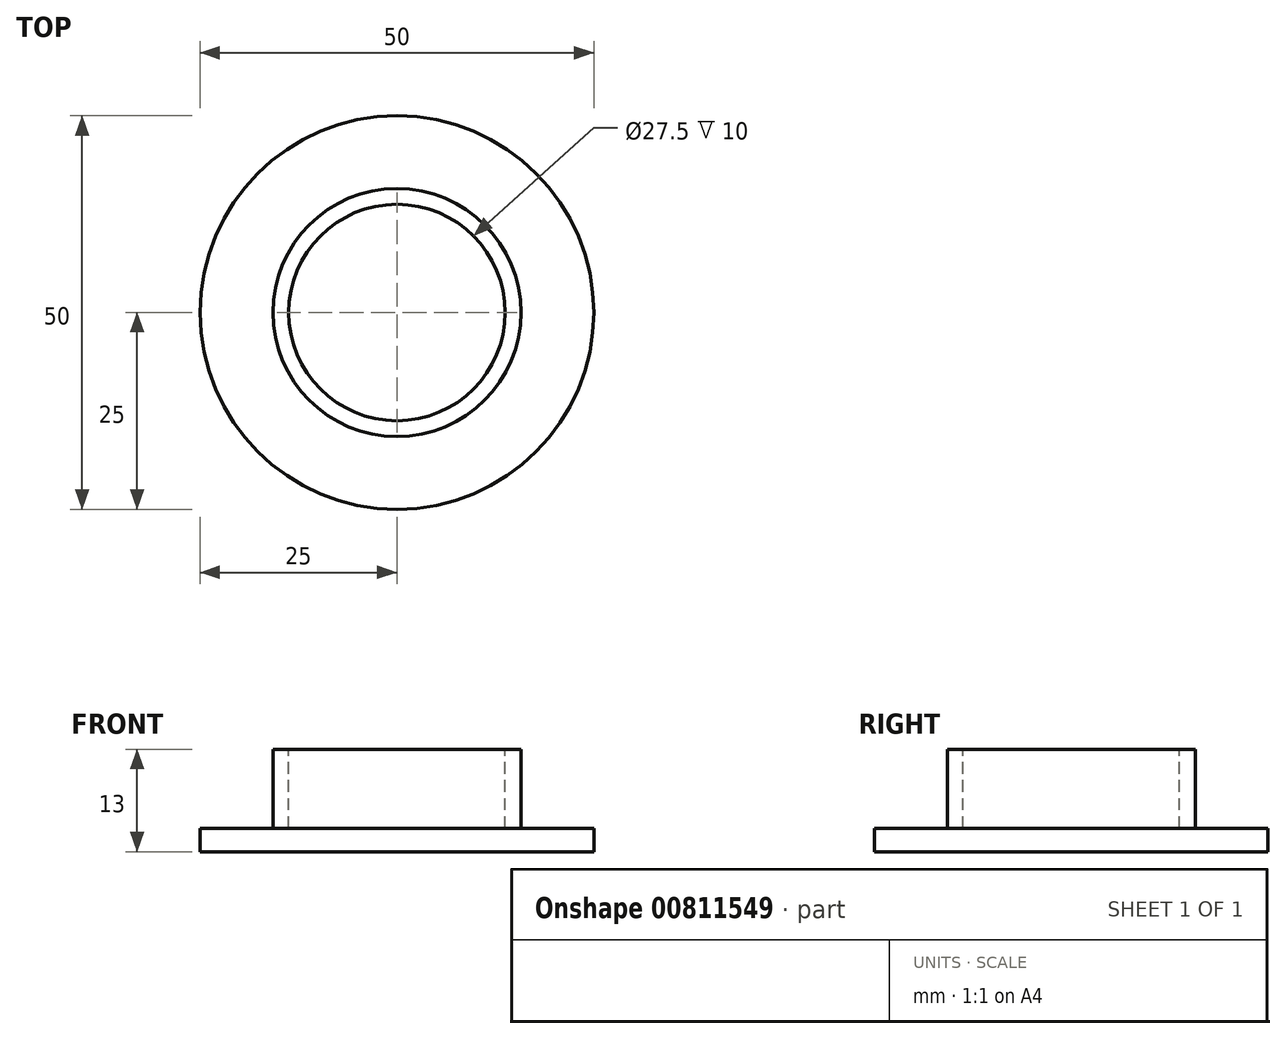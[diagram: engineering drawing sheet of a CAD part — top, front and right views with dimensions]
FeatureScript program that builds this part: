
annotation { "Feature Type Name" : "Feature", "Feature Type Description" : "" }
export const myFeature = defineFeature(function(context is Context, id is Id, definition is map)
    precondition{}
    {
        {
            var Q0;
            Q0=qCreatedBy(makeId("Top.planeOp"),FACE);
            var sketch = newSketch(context, id + "F0", { "sketchPlane" : qUnion([Q0])});
            skCircle(sketch, "E0", {"center": v(0, 0) * mm, "radius": 25 * mm});
            skSolve(sketch);
        }
        {
            var Q0;
            Q0=makeQuery(id+"F0.imprint","IMPRINT",FACE,{"disambiguationData":[TD([[makeQuery(id+"F0.imprint","IMPRINT",EDGE,{"derivedFrom":sQuery(id+"F0.wireOp",EDGE,"E0")}),1.0]])]});
            extrude(context, id + "F1", {"entities" : qUnion([Q0]), "depth" : 3 * mm, "offsetDistance" : 25 * mm});
        }
        {
            var Q0;
            Q0=makeQuery(id+"F1.opExtrude","CAP_FACE",FACE,{"disambiguationData":[OSD([sQuery(id+"F0.wireOp",EDGE,"E0")])],"isStart":false});
            var sketch = newSketch(context, id + "F2", { "sketchPlane" : qUnion([Q0])});
            skCircle(sketch, "E1", {"center": v(0, 0) * mm, "radius": 15.75 * mm});
            skSolve(sketch);
        }
        {
            var Q0;
            Q0=qSketchRegion(id+"F2",true);
            extrude(context, id + "F3", {"entities" : qUnion([Q0]), "operationType" : NewBodyOperationType.ADD, "depth" : 10 * mm, "offsetDistance" : 25 * mm});
        }
        {
            var Q0;
            Q0=makeQuery(id+"F3.opExtrude","CAP_FACE",FACE,{"disambiguationData":[OSD([sQuery(id+"F2.wireOp",EDGE,"E1")])],"isStart":false});
            var sketch = newSketch(context, id + "F4", { "sketchPlane" : qUnion([Q0])});
            skCircle(sketch, "E2", {"center": v(0, 0) * mm, "radius": 13.75 * mm});
            skSolve(sketch);
        }
        {
            var Q0;
            Q0=qSketchRegion(id+"F4",true);
            var Q1;
            Q1=makeQuery(id+"F1.opExtrude","CAP_FACE",FACE,{"disambiguationData":[OSD([sQuery(id+"F0.wireOp",EDGE,"E0")])],"isStart":false});
            extrude(context, id + "F5", {"entities" : qUnion([Q0]), "operationType" : NewBodyOperationType.REMOVE, "endBound" : BoundingType.UP_TO_SURFACE, "oppositeDirection" : true, "depth" : 25 * mm, "endBoundEntityFace" : qUnion([Q1]), "offsetDistance" : 3 * mm});
        }
    });
